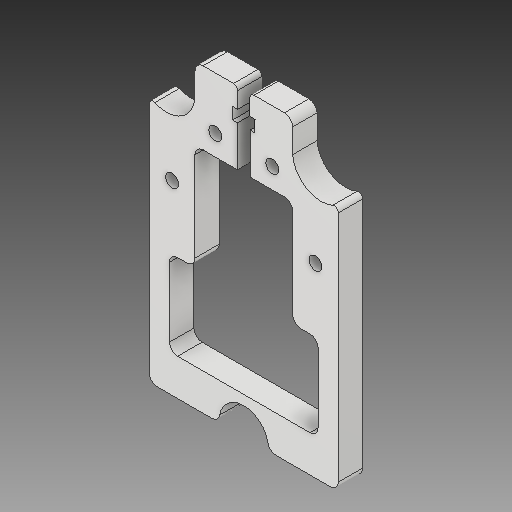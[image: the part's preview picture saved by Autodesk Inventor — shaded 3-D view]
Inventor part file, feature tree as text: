
AUTODESK INVENTOR PART (.ipt)
format: ipt  version: 2017 (Build 210142000, 142)  size: 192,512 bytes
history: native  units: mm
features: other x3, sketch x2
ambient origin geometry x8: Origin, YZ Plane, XZ Plane, XY Plane, X Axis, Y Axis, Z Axis, Center Point
bodies: Solid1 (feature_tree)
feature tree (5):
  other  "Hotend Slide Part 2.ipt"
  other  "Solid1::Hotend Slide Part 2.ipt"
  other  "TaggingFeature1"
  sketch  "Sketch1"  dims[d0=10.0mm]
  sketch  "Sketch2"
